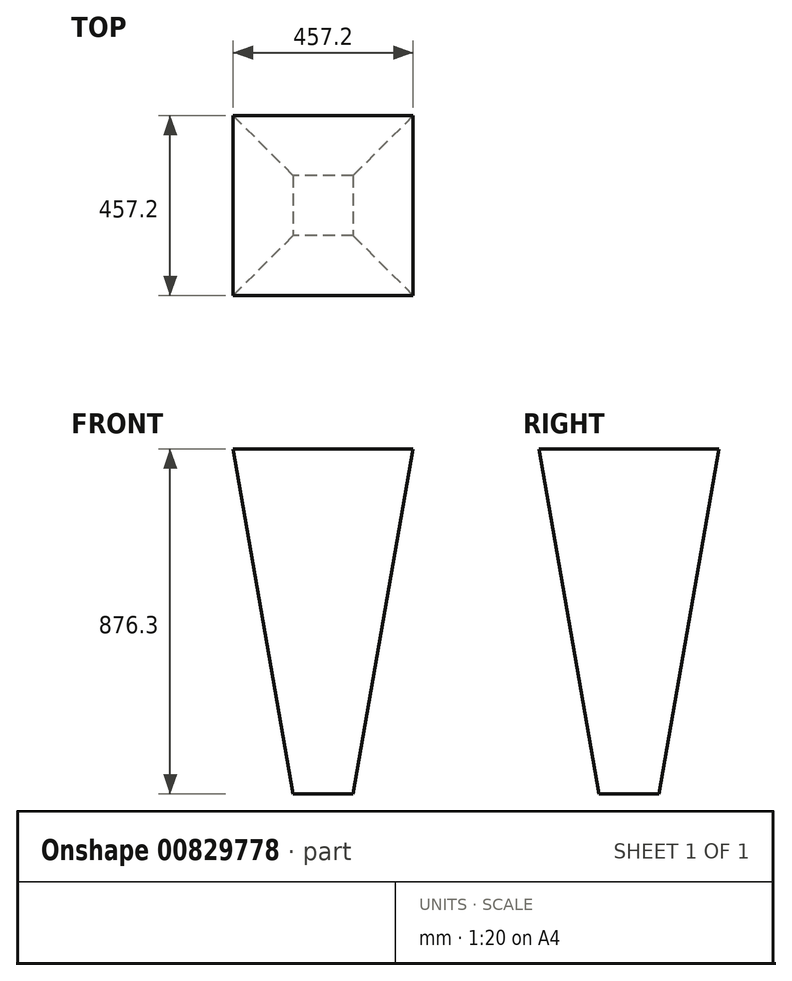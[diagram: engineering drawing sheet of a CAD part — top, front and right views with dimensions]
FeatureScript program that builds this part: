
annotation { "Feature Type Name" : "Feature", "Feature Type Description" : "" }
export const myFeature = defineFeature(function(context is Context, id is Id, definition is map)
    precondition{}
    {
        {
            var Q0;
            Q0=qCreatedBy(makeId("Top.planeOp"),FACE);
            var sketch = newSketch(context, id + "F0", { "sketchPlane" : qUnion([Q0])});
            skCircle(sketch, "E0", {"center": v(0, 0) * mm, "radius": 228.6 * mm, "construction": true});
            skLineSegment(sketch, "E1.bottom", {"start": v(76.2, 76.2) * mm, "end": v(-76.2, 76.2) * mm});
            skLineSegment(sketch, "E1.top", {"start": v(76.2, -76.2) * mm, "end": v(-76.2, -76.2) * mm});
            skLineSegment(sketch, "E1.left", {"start": v(76.2, 76.2) * mm, "end": v(76.2, -76.2) * mm});
            skLineSegment(sketch, "E1.right", {"start": v(-76.2, 76.2) * mm, "end": v(-76.2, -76.2) * mm});
            skSolve(sketch);
        }
        {
            var Q0;
            Q0=qCreatedBy(makeId("Top.planeOp"),FACE);
            cPlane(context, id + "F1", {"entities" : qUnion([Q0]), "cplaneType" : CPlaneType.OFFSET, "offset" : 876.3 * mm, "width" : 152.4 * mm, "height" : 152.4 * mm});
        }
        {
            var Q0;
            Q0=qCreatedBy(id+"F1.planeOp",FACE);
            var sketch = newSketch(context, id + "F2", { "sketchPlane" : qUnion([Q0])});
            skCircle(sketch, "E2", {"center": v(0, 0) * mm, "radius": 457.2 * mm, "construction": true});
            skLineSegment(sketch, "E3.bottom", {"start": v(228.6, 228.6) * mm, "end": v(-228.6, 228.6) * mm});
            skLineSegment(sketch, "E3.top", {"start": v(228.6, -228.6) * mm, "end": v(-228.6, -228.6) * mm});
            skLineSegment(sketch, "E3.left", {"start": v(228.6, 228.6) * mm, "end": v(228.6, -228.6) * mm});
            skLineSegment(sketch, "E3.right", {"start": v(-228.6, 228.6) * mm, "end": v(-228.6, -228.6) * mm});
            skSolve(sketch);
        }
        {
            var Q0;
            Q0=makeQuery(id+"F2.imprint","IMPRINT",FACE,{"disambiguationData":[TD([[makeQuery(id+"F2.imprint","IMPRINT",EDGE,{"derivedFrom":sQuery(id+"F2.wireOp",EDGE,"E3.bottom")}),1.0]])]});
            var Q1;
            Q1=makeQuery(id+"F0.imprint","IMPRINT",FACE,{"disambiguationData":[TD([[makeQuery(id+"F0.imprint","IMPRINT",EDGE,{"derivedFrom":sQuery(id+"F0.wireOp",EDGE,"E1.bottom")}),1.0]])]});
            loft(context, id + "F3", {"sheetProfilesArray" : [{ "sheetProfileEntities" : qUnion([Q0]) }, { "sheetProfileEntities" : qUnion([Q1]) }]});
        }
    });
